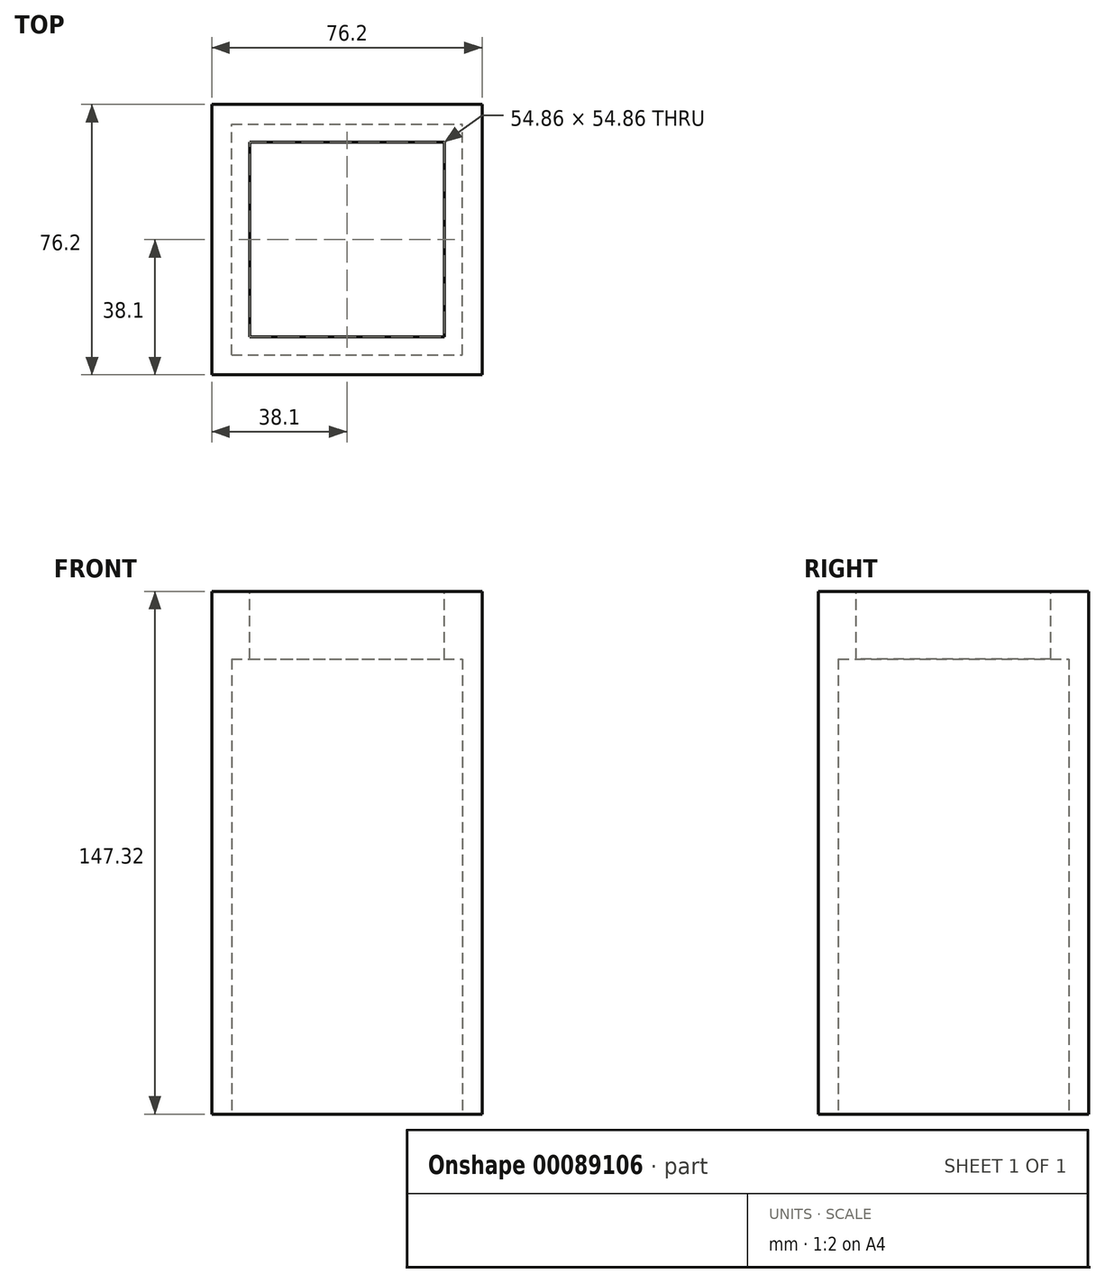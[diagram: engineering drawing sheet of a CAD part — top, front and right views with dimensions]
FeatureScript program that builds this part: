
annotation { "Feature Type Name" : "Feature", "Feature Type Description" : "" }
export const myFeature = defineFeature(function(context is Context, id is Id, definition is map)
    precondition{}
    {
        {
            var Q0;
            Q0=qCreatedBy(makeId("Top.planeOp"),FACE);
            var sketch = newSketch(context, id + "F0", { "sketchPlane" : qUnion([Q0])});
            skLineSegment(sketch, "E0.bottom", {"start": v(-38.1, -38.1) * mm, "end": v(38.1, -38.1) * mm});
            skLineSegment(sketch, "E0.top", {"start": v(-38.1, 38.1) * mm, "end": v(38.1, 38.1) * mm});
            skLineSegment(sketch, "E0.left", {"start": v(-38.1, -38.1) * mm, "end": v(-38.1, 38.1) * mm});
            skLineSegment(sketch, "E0.right", {"start": v(38.1, -38.1) * mm, "end": v(38.1, 38.1) * mm});
            skLineSegment(sketch, "E1.bottom", {"start": v(-32.51, -32.51) * mm, "end": v(32.51, -32.51) * mm});
            skLineSegment(sketch, "E1.top", {"start": v(-32.51, 32.51) * mm, "end": v(32.51, 32.51) * mm});
            skLineSegment(sketch, "E1.left", {"start": v(-32.51, -32.51) * mm, "end": v(-32.51, 32.51) * mm});
            skLineSegment(sketch, "E1.right", {"start": v(32.51, -32.51) * mm, "end": v(32.51, 32.51) * mm});
            skSolve(sketch);
        }
        {
            var Q0;
            Q0 = qSketchRegion(id + "F0", true);
            extrude(context, id + "F1", {"entities" : qUnion([Q0]), "depth" : 147.32 * mm});
        }
        {
            var Q0;
            Q0=makeQuery(id+"F1.opExtrude","CAP_FACE",FACE,{"disambiguationData":[OSD([sQuery(id+"F0.wireOp",EDGE,"E0.bottom"),sQuery(id+"F0.wireOp",EDGE,"E0.top"),sQuery(id+"F0.wireOp",EDGE,"E0.left"),sQuery(id+"F0.wireOp",EDGE,"E0.right"),sQuery(id+"F0.wireOp",EDGE,"E1.bottom"),sQuery(id+"F0.wireOp",EDGE,"E1.top"),sQuery(id+"F0.wireOp",EDGE,"E1.left"),sQuery(id+"F0.wireOp",EDGE,"E1.right")])],"isStart":false});
            var sketch = newSketch(context, id + "F2", { "sketchPlane" : qUnion([Q0])});
            skLineSegment(sketch, "E2.bottom", {"start": v(-38.1, 38.1) * mm, "end": v(38.1, 38.1) * mm});
            skLineSegment(sketch, "E2.top", {"start": v(-38.1, -38.1) * mm, "end": v(38.1, -38.1) * mm});
            skLineSegment(sketch, "E2.left", {"start": v(-38.1, 38.1) * mm, "end": v(-38.1, -38.1) * mm});
            skLineSegment(sketch, "E2.right", {"start": v(38.1, 38.1) * mm, "end": v(38.1, -38.1) * mm});
            skLineSegment(sketch, "E3.bottom", {"start": v(-27.43, 27.43) * mm, "end": v(27.43, 27.43) * mm});
            skLineSegment(sketch, "E3.top", {"start": v(-27.43, -27.43) * mm, "end": v(27.43, -27.43) * mm});
            skLineSegment(sketch, "E3.left", {"start": v(-27.43, 27.43) * mm, "end": v(-27.43, -27.43) * mm});
            skLineSegment(sketch, "E3.right", {"start": v(27.43, 27.43) * mm, "end": v(27.43, -27.43) * mm});
            skSolve(sketch);
        }
        {
            var Q0;
            Q0 = qSketchRegion(id + "F2", true);
            extrude(context, id + "F3", {"entities" : qUnion([Q0]), "operationType" : NewBodyOperationType.ADD, "oppositeDirection" : true, "depth" : 19.05 * mm});
        }
    });
